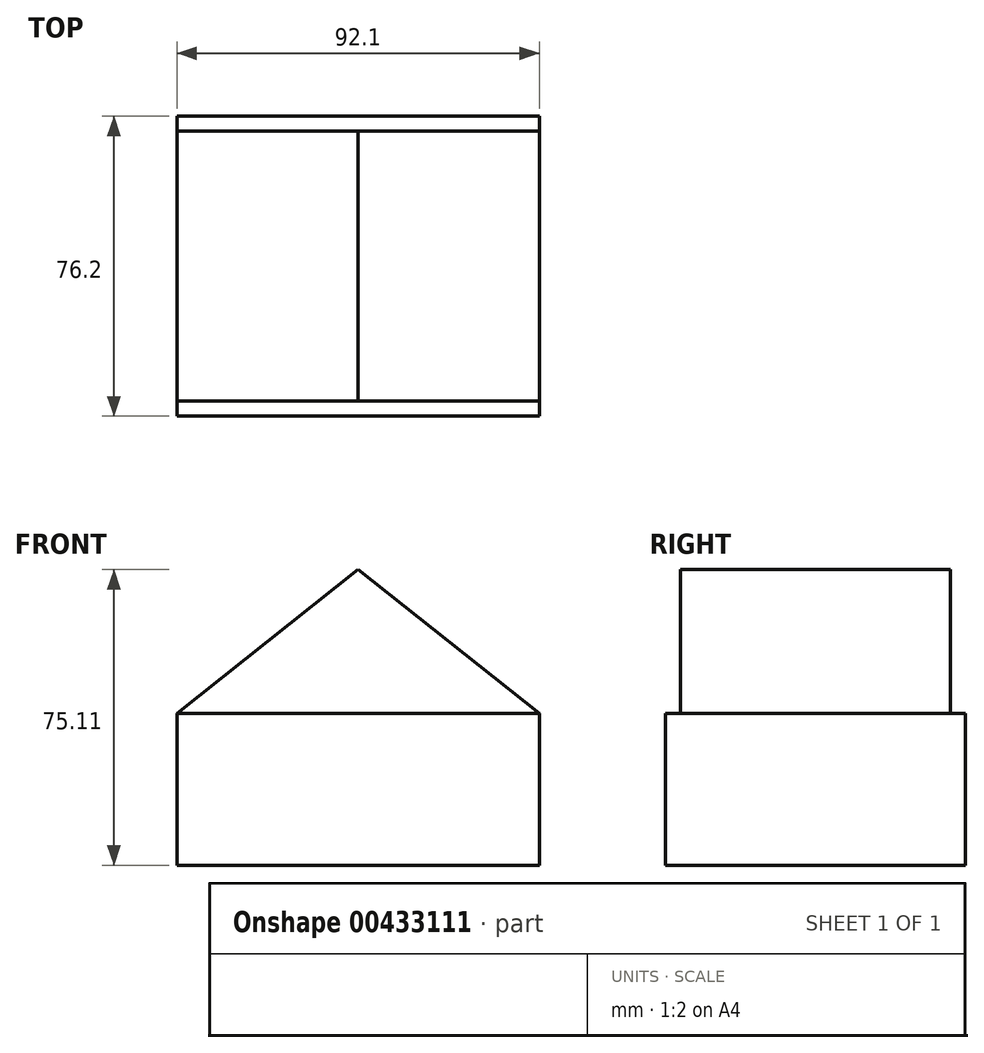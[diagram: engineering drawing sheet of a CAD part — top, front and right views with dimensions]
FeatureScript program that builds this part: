
annotation { "Feature Type Name" : "Feature", "Feature Type Description" : "" }
export const myFeature = defineFeature(function(context is Context, id is Id, definition is map)
    precondition{}
    {
        {
            var Q0;
            Q0=qCreatedBy(makeId("Front.planeOp"),FACE);
            var sketch = newSketch(context, id + "F0", { "sketchPlane" : qUnion([Q0])});
            skLineSegment(sketch, "E0.bottom", {"start": v(-46.05, 19.28) * mm, "end": v(46.05, 19.28) * mm});
            skLineSegment(sketch, "E0.top", {"start": v(-46.05, -19.28) * mm, "end": v(46.05, -19.28) * mm});
            skLineSegment(sketch, "E0.left", {"start": v(-46.05, 19.28) * mm, "end": v(-46.05, -19.28) * mm});
            skLineSegment(sketch, "E0.right", {"start": v(46.05, 19.28) * mm, "end": v(46.05, -19.28) * mm});
            skPoint(sketch, "E0.middle", {"position": v(0, 0) * mm});
            skLineSegment(sketch, "E1", {"start": v(-46.05, 19.28) * mm, "end": v(0, 55.83) * mm});
            skLineSegment(sketch, "E2", {"start": v(46.05, 19.28) * mm, "end": v(0, 55.83) * mm});
            skSolve(sketch);
        }
        {
            var Q0;
            Q0=makeQuery(id+"F0.imprint","IMPRINT",FACE,{"disambiguationData":[TD([[makeQuery(id+"F0.imprint","IMPRINT",EDGE,{"derivedFrom":sQuery(id+"F0.wireOp",EDGE,"E0.bottom")}),1.0]])]});
            extrude(context, id + "F1", {"entities" : qUnion([Q0]), "endBound" : BoundingType.SYMMETRIC, "depth" : 68.58 * mm});
        }
        {
            var Q0;
            Q0=makeQuery(id+"F0.imprint","IMPRINT",FACE,{"disambiguationData":[TD([[makeQuery(id+"F0.imprint","IMPRINT",EDGE,{"derivedFrom":sQuery(id+"F0.wireOp",EDGE,"E0.bottom")}),-1.0]])]});
            extrude(context, id + "F2", {"entities" : qUnion([Q0]), "operationType" : NewBodyOperationType.ADD, "endBound" : BoundingType.SYMMETRIC, "depth" : 76.2 * mm});
        }
    });
